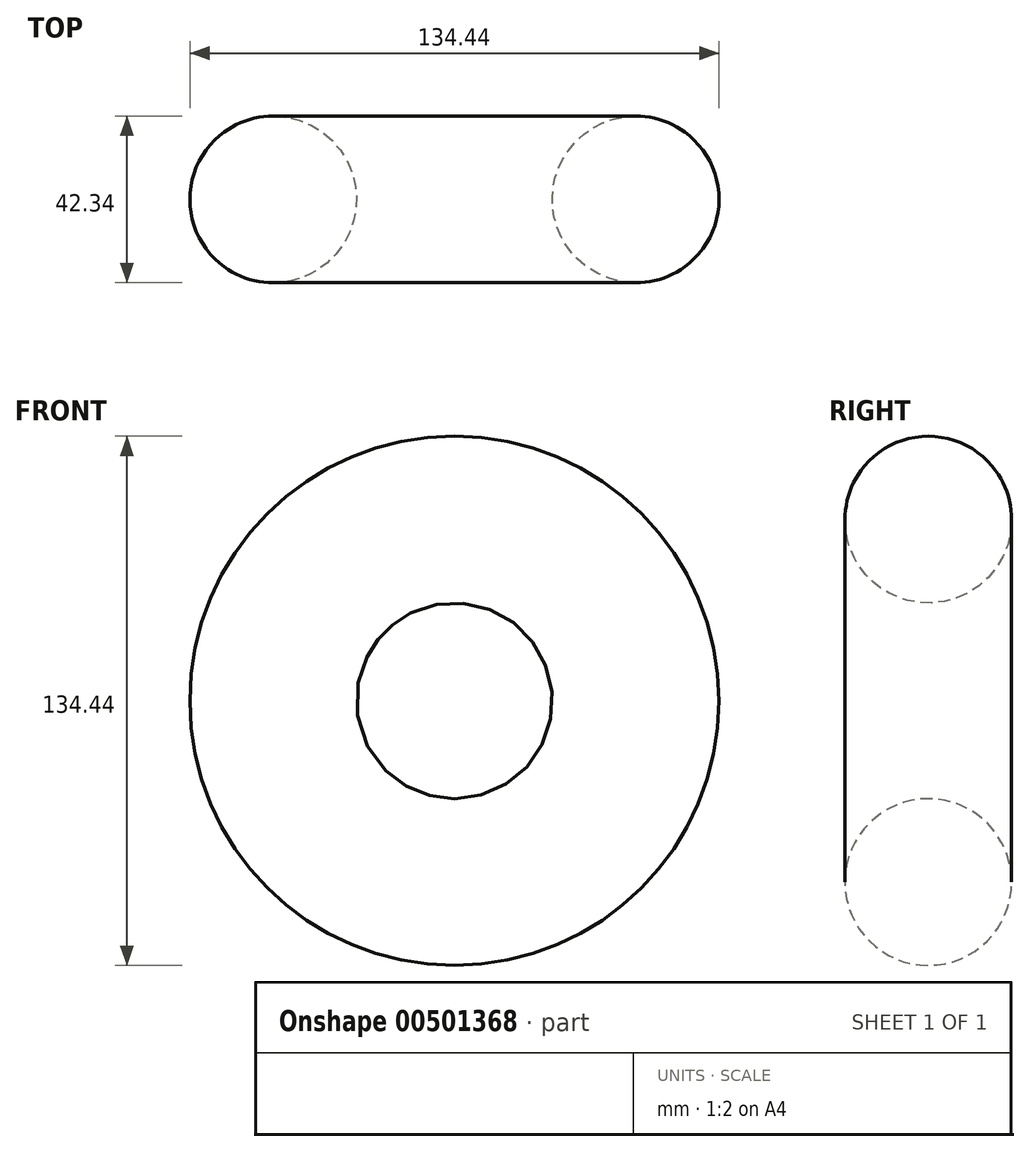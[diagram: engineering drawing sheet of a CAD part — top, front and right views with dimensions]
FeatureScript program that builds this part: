
annotation { "Feature Type Name" : "Feature", "Feature Type Description" : "" }
export const myFeature = defineFeature(function(context is Context, id is Id, definition is map)
    precondition{}
    {
        {
            var Q0;
            Q0=qCreatedBy(makeId("Top.planeOp"),FACE);
            var sketch = newSketch(context, id + "F0", { "sketchPlane" : qUnion([Q0])});
            skCircle(sketch, "E0", {"center": v(46.05, 21.3) * mm, "radius": 21.17 * mm});
            skLineSegment(sketch, "E1", {"start": v(0, 0) * mm, "end": v(0, 47.2) * mm, "construction": true});
            skSolve(sketch);
        }
        {
            var Q0;
            Q0=makeQuery(id+"F0.imprint","IMPRINT",FACE,{"disambiguationData":[TD([[makeQuery(id+"F0.imprint","IMPRINT",EDGE,{"derivedFrom":sQuery(id+"F0.wireOp",EDGE,"E0")}),1.0]])]});
            var Q1;
            Q1=sQuery(id+"F0.wireOp",EDGE,"E1");
            revolve(context, id + "F1", {"entities" : qUnion([Q0]), "axis" : qUnion([Q1]), "revolveType" : RevolveType.FULL});
        }
    });
